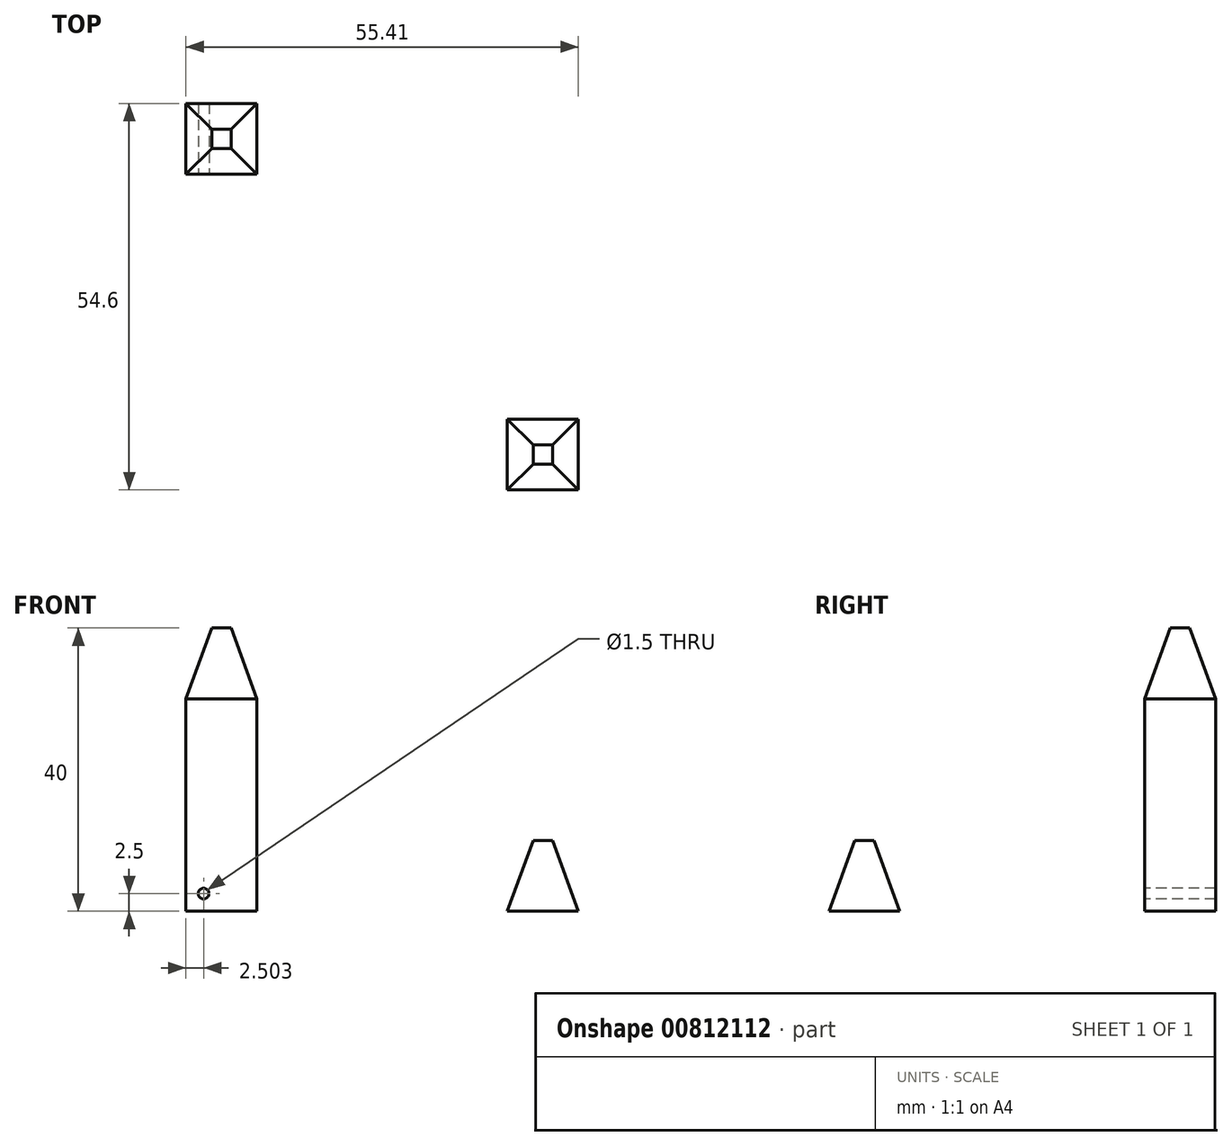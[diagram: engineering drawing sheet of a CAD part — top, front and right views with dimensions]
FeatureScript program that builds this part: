
annotation { "Feature Type Name" : "Feature", "Feature Type Description" : "" }
export const myFeature = defineFeature(function(context is Context, id is Id, definition is map)
    precondition{}
    {
        {
            var Q0;
            Q0=qCreatedBy(makeId("Top.planeOp"),FACE);
            var sketch = newSketch(context, id + "F0", { "sketchPlane" : qUnion([Q0])});
            skLineSegment(sketch, "E0.bottom", {"start": v(-29.66, 0) * mm, "end": v(-19.66, 0) * mm});
            skLineSegment(sketch, "E0.top", {"start": v(-29.66, 10) * mm, "end": v(-19.66, 10) * mm});
            skLineSegment(sketch, "E0.left", {"start": v(-29.66, 0) * mm, "end": v(-29.66, 10) * mm});
            skLineSegment(sketch, "E0.right", {"start": v(-19.66, 0) * mm, "end": v(-19.66, 10) * mm});
            skSolve(sketch);
        }
        {
            var Q0;
            Q0=qSketchRegion(id+"F0",true);
            extrude(context, id + "F1", {"entities" : qUnion([Q0]), "depth" : 30 * mm, "offsetDistance" : 25 * mm});
        }
        {
            var Q0;
            Q0=qCreatedBy(makeId("Top.planeOp"),FACE);
            var sketch = newSketch(context, id + "F2", { "sketchPlane" : qUnion([Q0])});
            skLineSegment(sketch, "E1.bottom", {"start": v(15.75, -34.6) * mm, "end": v(25.75, -34.6) * mm});
            skLineSegment(sketch, "E1.top", {"start": v(15.75, -44.6) * mm, "end": v(25.75, -44.6) * mm});
            skLineSegment(sketch, "E1.left", {"start": v(15.75, -34.6) * mm, "end": v(15.75, -44.6) * mm});
            skLineSegment(sketch, "E1.right", {"start": v(25.75, -34.6) * mm, "end": v(25.75, -44.6) * mm});
            skSolve(sketch);
        }
        {
            var Q0;
            Q0=qSketchRegion(id+"F2",true);
            extrude(context, id + "F3", {"entities" : qUnion([Q0]), "depth" : 10 * mm, "hasDraft" : true, "draftAngle" : 20 * degree, "draftPullDirection" : true});
        }
        {
            var Q0;
            Q0=makeQuery(id+"F1.opExtrude","SWEPT_FACE",FACE,{"disambiguationData":[OSD([sQuery(id+"F0.wireOp",EDGE,"E0.bottom")])]});
            var sketch = newSketch(context, id + "F4", { "sketchPlane" : qUnion([Q0])});
            skCircle(sketch, "E2", {"center": v(-27.16, 2.5) * mm, "radius": 0.75 * mm});
            skSolve(sketch);
        }
        {
            var Q0;
            Q0=qSketchRegion(id+"F4",true);
            extrude(context, id + "F5", {"entities" : qUnion([Q0]), "operationType" : NewBodyOperationType.REMOVE, "oppositeDirection" : true, "depth" : 25 * mm});
        }
        {
            var Q0;
            Q0=makeQuery(id+"F1.opExtrude","CAP_FACE",FACE,{"disambiguationData":[OSD([sQuery(id+"F0.wireOp",EDGE,"E0.bottom"),sQuery(id+"F0.wireOp",EDGE,"E0.top"),sQuery(id+"F0.wireOp",EDGE,"E0.left"),sQuery(id+"F0.wireOp",EDGE,"E0.right")])],"isStart":false});
            var sketch = newSketch(context, id + "F6", { "sketchPlane" : qUnion([Q0])});
            skLineSegment(sketch, "E3.bottom", {"start": v(-29.66, 10) * mm, "end": v(-19.66, 10) * mm});
            skLineSegment(sketch, "E3.top", {"start": v(-29.66, 0) * mm, "end": v(-19.66, 0) * mm});
            skLineSegment(sketch, "E3.left", {"start": v(-29.66, 10) * mm, "end": v(-29.66, 0) * mm});
            skLineSegment(sketch, "E3.right", {"start": v(-19.66, 10) * mm, "end": v(-19.66, 0) * mm});
            skSolve(sketch);
        }
        {
            var Q0;
            Q0 = qSketchRegion(id + "F6", true);
            extrude(context, id + "F7", {"entities" : qUnion([Q0]), "operationType" : NewBodyOperationType.ADD, "depth" : 10 * mm, "offsetDistance" : 25 * mm, "hasDraft" : true, "draftAngle" : 20 * degree, "draftPullDirection" : true});
        }
    });
